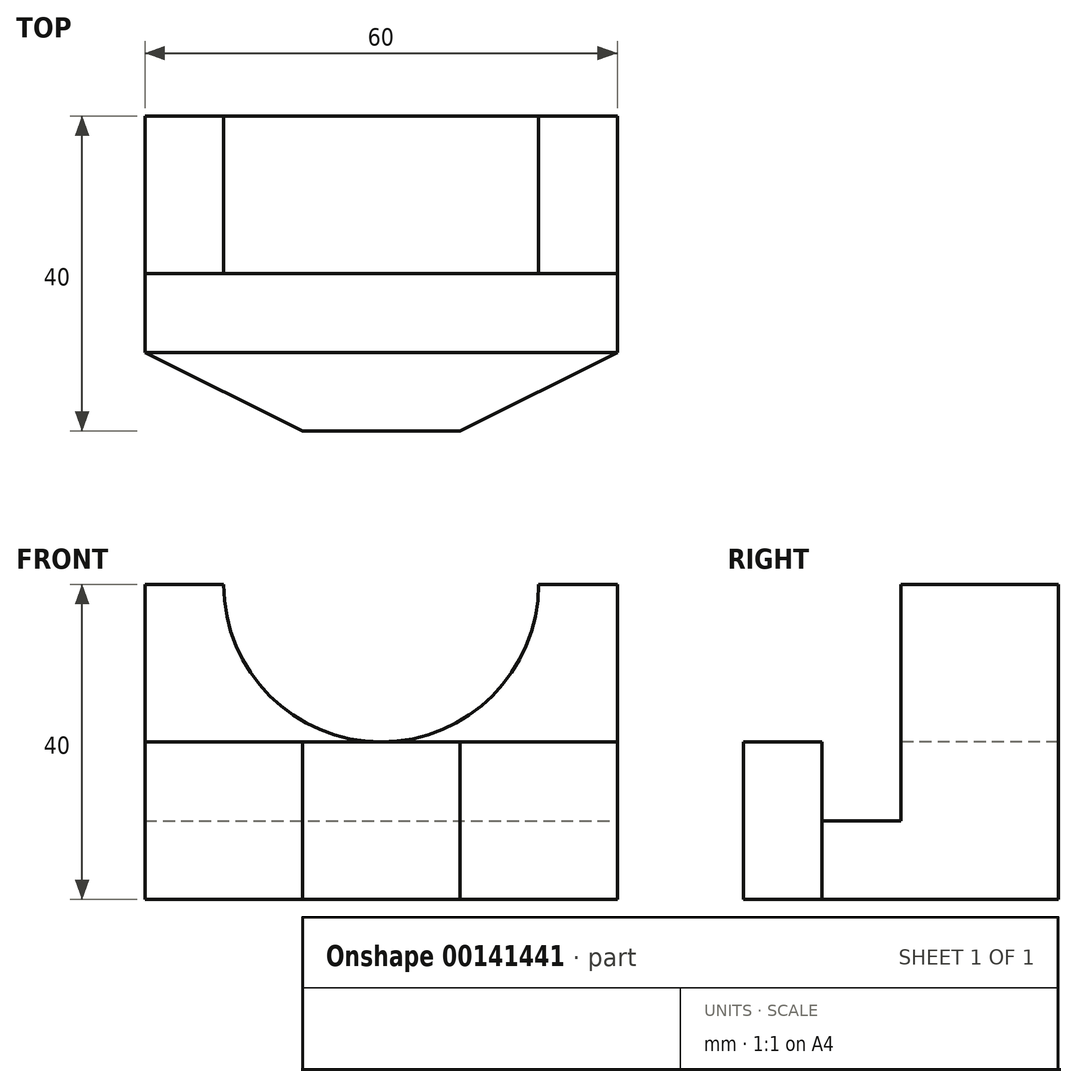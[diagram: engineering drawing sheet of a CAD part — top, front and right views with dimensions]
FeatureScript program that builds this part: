
annotation { "Feature Type Name" : "Feature", "Feature Type Description" : "" }
export const myFeature = defineFeature(function(context is Context, id is Id, definition is map)
    precondition{}
    {
        {
            var Q0;
            Q0=qCreatedBy(makeId("Front.planeOp"),FACE);
            var sketch = newSketch(context, id + "F0", { "sketchPlane" : qUnion([Q0])});
            skLineSegment(sketch, "E0.bottom", {"start": v(0, 0) * mm, "end": v(60, 0) * mm});
            skLineSegment(sketch, "E0.top", {"start": v(0, 40) * mm, "end": v(60, 40) * mm});
            skLineSegment(sketch, "E0.left", {"start": v(0, 0) * mm, "end": v(0, 40) * mm});
            skLineSegment(sketch, "E0.right", {"start": v(60, 0) * mm, "end": v(60, 40) * mm});
            skSolve(sketch);
        }
        {
            var Q0;
            Q0 = qSketchRegion(id + "F0", true);
            extrude(context, id + "F1", {"entities" : qUnion([Q0]), "depth" : 20 * mm});
        }
        {
            var Q0;
            Q0=makeQuery(id+"F1.opExtrude","CAP_FACE",FACE,{"disambiguationData":[OSD([sQuery(id+"F0.wireOp",EDGE,"E0.bottom"),sQuery(id+"F0.wireOp",EDGE,"E0.top"),sQuery(id+"F0.wireOp",EDGE,"E0.left"),sQuery(id+"F0.wireOp",EDGE,"E0.right")])],"isStart":false});
            var sketch = newSketch(context, id + "F2", { "sketchPlane" : qUnion([Q0])});
            skLineSegment(sketch, "E1", {"start": v(10, 40) * mm, "end": v(50, 40) * mm});
            skArc(sketch, "E2", {"start": v(10, 40) * mm, "mid": v(30, 20) * mm, "end": v(50, 40) * mm});
            skSolve(sketch);
        }
        {
            var Q0;
            Q0 = qSketchRegion(id + "F2", true);
            extrude(context, id + "F3", {"entities" : qUnion([Q0]), "operationType" : NewBodyOperationType.REMOVE, "oppositeDirection" : true, "depth" : 20 * mm});
        }
        {
            var Q0;
            Q0=makeQuery(id+"F1.opExtrude","CAP_FACE",FACE,{"disambiguationData":[OSD([sQuery(id+"F0.wireOp",EDGE,"E0.bottom"),sQuery(id+"F0.wireOp",EDGE,"E0.top"),sQuery(id+"F0.wireOp",EDGE,"E0.left"),sQuery(id+"F0.wireOp",EDGE,"E0.right")])],"isStart":false});
            var sketch = newSketch(context, id + "F4", { "sketchPlane" : qUnion([Q0])});
            skLineSegment(sketch, "E3.bottom", {"start": v(0, 0) * mm, "end": v(60, 0) * mm});
            skLineSegment(sketch, "E3.top", {"start": v(0, 10) * mm, "end": v(60, 10) * mm});
            skLineSegment(sketch, "E3.left", {"start": v(0, 0) * mm, "end": v(0, 10) * mm});
            skLineSegment(sketch, "E3.right", {"start": v(60, 0) * mm, "end": v(60, 10) * mm});
            skSolve(sketch);
        }
        {
            var Q0;
            Q0 = qSketchRegion(id + "F4", true);
            extrude(context, id + "F5", {"entities" : qUnion([Q0]), "operationType" : NewBodyOperationType.ADD, "depth" : 10 * mm});
        }
        {
            var Q0;
            Q0=makeQuery(id+"F5.opExtrude","CAP_FACE",FACE,{"disambiguationData":[OSD([sQuery(id+"F4.wireOp",EDGE,"E3.bottom"),sQuery(id+"F4.wireOp",EDGE,"E3.top"),sQuery(id+"F4.wireOp",EDGE,"E3.left"),sQuery(id+"F4.wireOp",EDGE,"E3.right")])],"isStart":false});
            var sketch = newSketch(context, id + "F6", { "sketchPlane" : qUnion([Q0])});
            skLineSegment(sketch, "E4.bottom", {"start": v(0, 0) * mm, "end": v(60, 0) * mm});
            skLineSegment(sketch, "E4.top", {"start": v(0, 20) * mm, "end": v(60, 20) * mm});
            skLineSegment(sketch, "E4.left", {"start": v(0, 0) * mm, "end": v(0, 20) * mm});
            skLineSegment(sketch, "E4.right", {"start": v(60, 0) * mm, "end": v(60, 20) * mm});
            skSolve(sketch);
        }
        {
            var Q0;
            Q0 = qSketchRegion(id + "F6", true);
            extrude(context, id + "F7", {"entities" : qUnion([Q0]), "operationType" : NewBodyOperationType.ADD, "depth" : 10 * mm});
        }
        {
            var Q0;
            Q0=makeQuery(id+"F7.opExtrude","SWEPT_FACE",FACE,{"disambiguationData":[OSD([sQuery(id+"F6.wireOp",EDGE,"E4.top")])]});
            var sketch = newSketch(context, id + "F8", { "sketchPlane" : qUnion([Q0])});
            skLineSegment(sketch, "E5", {"start": v(60, -40) * mm, "end": v(60, -30) * mm});
            skLineSegment(sketch, "E6", {"start": v(60, -30) * mm, "end": v(40, -40) * mm});
            skLineSegment(sketch, "E7", {"start": v(40, -40) * mm, "end": v(60, -40) * mm});
            skLineSegment(sketch, "E8", {"start": v(0, -40) * mm, "end": v(0, -30) * mm});
            skLineSegment(sketch, "E9", {"start": v(0, -30) * mm, "end": v(20, -40) * mm});
            skLineSegment(sketch, "E10", {"start": v(20, -40) * mm, "end": v(0, -40) * mm});
            skSolve(sketch);
        }
        {
            var Q0;
            Q0 = qSketchRegion(id + "F8", true);
            extrude(context, id + "F9", {"entities" : qUnion([Q0]), "operationType" : NewBodyOperationType.REMOVE, "oppositeDirection" : true, "depth" : 20 * mm});
        }
    });
